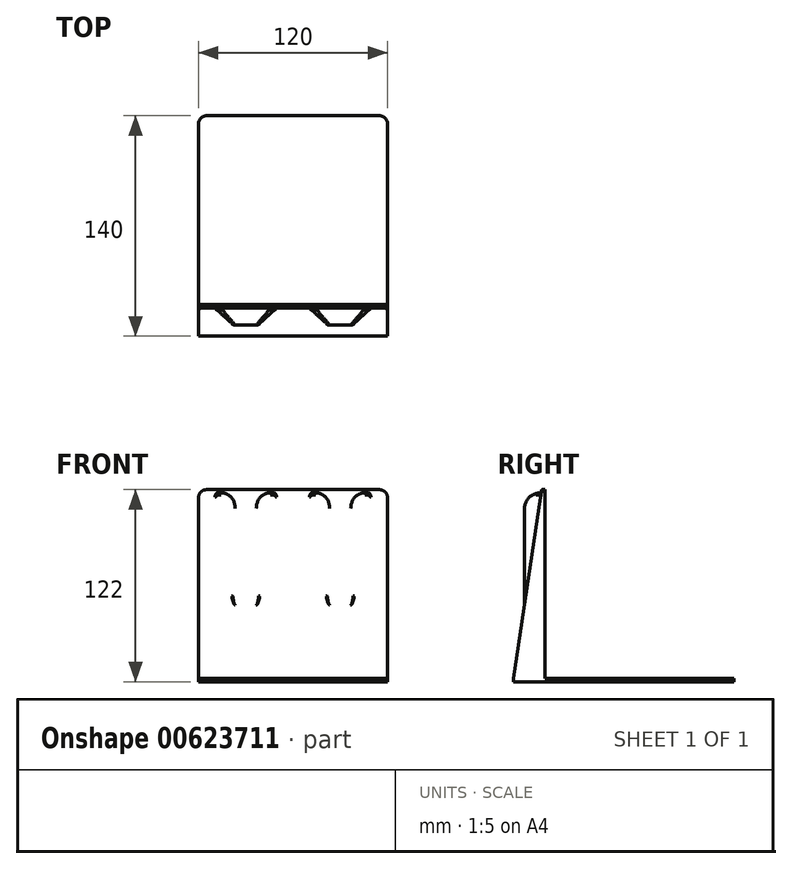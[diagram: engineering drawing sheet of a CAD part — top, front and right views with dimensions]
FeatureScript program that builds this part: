
annotation { "Feature Type Name" : "Feature", "Feature Type Description" : "" }
export const myFeature = defineFeature(function(context is Context, id is Id, definition is map)
    precondition{}
    {
        {
            var Q0;
            Q0=qCreatedBy(makeId("Right.planeOp"),FACE);
            var sketch = newSketch(context, id + "F0", { "sketchPlane" : qUnion([Q0])});
            skLineSegment(sketch, "E0", {"start": v(0, 120) * mm, "end": v(0, 0) * mm});
            skLineSegment(sketch, "E1", {"start": v(0, 0) * mm, "end": v(120, 0) * mm});
            skLineSegment(sketch, "E2", {"start": v(120, 0) * mm, "end": v(120, -2) * mm});
            skLineSegment(sketch, "E3", {"start": v(120, -2) * mm, "end": v(-20, -2) * mm});
            skLineSegment(sketch, "E4", {"start": v(-20, -2) * mm, "end": v(-20, 0) * mm});
            skLineSegment(sketch, "E5", {"start": v(-20, 0) * mm, "end": v(-2, 120) * mm});
            skLineSegment(sketch, "E6", {"start": v(-2, 120) * mm, "end": v(0, 120) * mm});
            skSolve(sketch);
        }
        {
            var Q0;
            Q0=makeQuery(id+"F0.imprint","IMPRINT",FACE,{"disambiguationData":[TD([[makeQuery(id+"F0.imprint","IMPRINT",EDGE,{"derivedFrom":sQuery(id+"F0.wireOp",EDGE,"E0")}),-1.0]])]});
            extrude(context, id + "F1", {"entities" : qUnion([Q0]), "depth" : 120 * mm, "offsetDistance" : 25 * mm});
        }
        {
            var Q0;
            Q0=makeQuery(id+"F1.opExtrude","SWEPT_FACE",FACE,{"disambiguationData":[OSD([sQuery(id+"F0.wireOp",EDGE,"E3")])]});
            var sketch = newSketch(context, id + "F2", { "sketchPlane" : qUnion([Q0])});
            skLineSegment(sketch, "E7.0", {"start": v(120, 20) * mm, "end": v(0, 20) * mm});
            skLineSegment(sketch, "E8.0", {"start": v(0, -120) * mm, "end": v(0, 20) * mm});
            skPoint(sketch, "E9.0", {"position": v(120, 0) * mm});
            skLineSegment(sketch, "E10.0.0", {"start": v(0, 20) * mm, "end": v(0, -120) * mm, "construction": true});
            skLineSegment(sketch, "E10.0.1", {"start": v(0, -120) * mm, "end": v(120, -120) * mm, "construction": true});
            skLineSegment(sketch, "E10.0.2", {"start": v(120, -120) * mm, "end": v(120, 20) * mm, "construction": true});
            skLineSegment(sketch, "E10.0.3", {"start": v(120, 20) * mm, "end": v(0, 20) * mm, "construction": true});
            skLineSegment(sketch, "E11", {"start": v(0, 0) * mm, "end": v(120, 0) * mm, "construction": true});
            skLineSegment(sketch, "E12.0", {"start": v(120, 2) * mm, "end": v(0, 2) * mm, "construction": true});
            skLineSegment(sketch, "E13", {"start": v(8, 0) * mm, "end": v(22.42, 12.99) * mm});
            skLineSegment(sketch, "E14", {"start": v(22.42, 12.99) * mm, "end": v(37.58, 12.99) * mm});
            skLineSegment(sketch, "E15", {"start": v(37.58, 12.99) * mm, "end": v(52, 0) * mm});
            skLineSegment(sketch, "E16", {"start": v(52, 0) * mm, "end": v(8, 0) * mm});
            skLineSegment(sketch, "E17", {"start": v(60, 20) * mm, "end": v(60, -38) * mm, "construction": true});
            skLineSegment(sketch, "E18.MirrorCS", {"start": v(82.42, 12.99) * mm, "end": v(68, 0) * mm});
            skLineSegment(sketch, "E19.MirrorCS", {"start": v(97.58, 12.99) * mm, "end": v(82.42, 12.99) * mm});
            skLineSegment(sketch, "E20.MirrorCS", {"start": v(112, 0) * mm, "end": v(97.58, 12.99) * mm});
            skLineSegment(sketch, "E21.MirrorCS", {"start": v(120, 0) * mm, "end": v(0, 0) * mm, "construction": true});
            skLineSegment(sketch, "E22", {"start": v(68, 0) * mm, "end": v(112, 0) * mm});
            skSolve(sketch);
        }
        {
            var Q0;
            Q0=makeQuery(id+"F2.imprint","IMPRINT",FACE,{"disambiguationData":[TD([[makeQuery(id+"F2.imprint","IMPRINT",EDGE,{"derivedFrom":sQuery(id+"F2.wireOp",EDGE,"E13")}),-1.0]])]});
            var Q1;
            Q1=makeQuery(id+"F2.imprint","IMPRINT",FACE,{"disambiguationData":[TD([[makeQuery(id+"F2.imprint","IMPRINT",EDGE,{"derivedFrom":sQuery(id+"F2.wireOp",EDGE,"E18.MirrorCS")}),1.0]])]});
            extrude(context, id + "F3", {"entities" : qUnion([Q0, Q1]), "operationType" : NewBodyOperationType.ADD, "oppositeDirection" : true, "depth" : 120 * mm, "offsetDistance" : 25 * mm});
        }
        {
            var Q0;
            Q0=makeQuery(id+"F3.opExtrude","CAP_EDGE",EDGE,{"disambiguationData":[OSD([sQuery(id+"F2.wireOp",EDGE,"E19.MirrorCS")])],"isStart":false});
            var Q1;
            Q1=makeQuery(id+"F3.opExtrude","CAP_EDGE",EDGE,{"disambiguationData":[OSD([sQuery(id+"F2.wireOp",EDGE,"E14")])],"isStart":false});
            fillet(context, id + "F4", {"entities" : qUnion([Q0, Q1]), "radius" : 10 * mm, "tangentPropagation" : true, "allowEdgeOverflow" : false});
        }
        {
            var Q0;
            Q0=makeQuery(id+"F3.opExtrude","SWEPT_EDGE",EDGE,{"disambiguationData":[OSD([sQuery(id+"F2.wireOp",EDGE,"E19.MirrorCS"),sQuery(id+"F2.wireOp",EDGE,"E20.MirrorCS")])]});
            var Q1;
            Q1=makeQuery(id+"F3.opExtrude","SWEPT_EDGE",EDGE,{"disambiguationData":[OSD([sQuery(id+"F2.wireOp",EDGE,"E18.MirrorCS"),sQuery(id+"F2.wireOp",EDGE,"E19.MirrorCS")])]});
            var Q2;
            Q2=makeQuery(id+"F3.opExtrude","SWEPT_EDGE",EDGE,{"disambiguationData":[OSD([sQuery(id+"F2.wireOp",EDGE,"E14"),sQuery(id+"F2.wireOp",EDGE,"E15")])]});
            var Q3;
            Q3=makeQuery(id+"F3.opExtrude","SWEPT_EDGE",EDGE,{"disambiguationData":[OSD([sQuery(id+"F2.wireOp",EDGE,"E13"),sQuery(id+"F2.wireOp",EDGE,"E14")])]});
            var Q4;
            Q4=makeQuery(id+"F4.opFillet","BLEND_EDGE",EDGE,{"blendedFrom":[makeQuery(id+"F3.opExtrude","CAP_EDGE",EDGE,{"disambiguationData":[OSD([sQuery(id+"F2.wireOp",EDGE,"E14")])],"isStart":false}),makeQuery(id+"F3.opExtrude","SWEPT_FACE",FACE,{"disambiguationData":[OSD([sQuery(id+"F2.wireOp",EDGE,"E13")])]})],"blendedInto":[makeQuery(id+"F3.opExtrude","SWEPT_FACE",FACE,{"disambiguationData":[OSD([sQuery(id+"F2.wireOp",EDGE,"E13")])]})]});
            var Q5;
            Q5=makeQuery(id+"F4.opFillet","BLEND_EDGE",EDGE,{"blendedFrom":[makeQuery(id+"F3.opExtrude","CAP_EDGE",EDGE,{"disambiguationData":[OSD([sQuery(id+"F2.wireOp",EDGE,"E14")])],"isStart":false}),makeQuery(id+"F3.opExtrude","SWEPT_FACE",FACE,{"disambiguationData":[OSD([sQuery(id+"F2.wireOp",EDGE,"E15")])]})],"blendedInto":[makeQuery(id+"F3.opExtrude","SWEPT_FACE",FACE,{"disambiguationData":[OSD([sQuery(id+"F2.wireOp",EDGE,"E15")])]})]});
            var Q6;
            Q6=makeQuery(id+"F4.opFillet","BLEND_EDGE",EDGE,{"blendedFrom":[makeQuery(id+"F3.opExtrude","CAP_EDGE",EDGE,{"disambiguationData":[OSD([sQuery(id+"F2.wireOp",EDGE,"E19.MirrorCS")])],"isStart":false}),makeQuery(id+"F3.opExtrude","SWEPT_FACE",FACE,{"disambiguationData":[OSD([sQuery(id+"F2.wireOp",EDGE,"E18.MirrorCS")])]})],"blendedInto":[makeQuery(id+"F3.opExtrude","SWEPT_FACE",FACE,{"disambiguationData":[OSD([sQuery(id+"F2.wireOp",EDGE,"E18.MirrorCS")])]})]});
            var Q7;
            Q7=makeQuery(id+"F4.opFillet","BLEND_EDGE",EDGE,{"blendedFrom":[makeQuery(id+"F3.opExtrude","CAP_EDGE",EDGE,{"disambiguationData":[OSD([sQuery(id+"F2.wireOp",EDGE,"E19.MirrorCS")])],"isStart":false}),makeQuery(id+"F3.opExtrude","SWEPT_FACE",FACE,{"disambiguationData":[OSD([sQuery(id+"F2.wireOp",EDGE,"E20.MirrorCS")])]})],"blendedInto":[makeQuery(id+"F3.opExtrude","SWEPT_FACE",FACE,{"disambiguationData":[OSD([sQuery(id+"F2.wireOp",EDGE,"E20.MirrorCS")])]})]});
            fillet(context, id + "F5", {"entities" : qUnion([Q0, Q1, Q2, Q3, Q4, Q5, Q6, Q7]), "radius" : 2.4 * mm, "tangentPropagation" : true, "allowEdgeOverflow" : false});
        }
        {
            var Q0;
            Q0=makeQuery(id+"F3.boolean.opBoolean","INTERSECT",EDGE,{"derivedFrom":[makeQuery(id+"F1.opExtrude","SWEPT_FACE",FACE,{"disambiguationData":[OSD([sQuery(id+"F0.wireOp",EDGE,"E5")])]}),makeQuery(id+"F3.opExtrude","SWEPT_FACE",FACE,{"disambiguationData":[OSD([sQuery(id+"F2.wireOp",EDGE,"E20.MirrorCS")])]})]});
            var Q1;
            Q1=makeQuery(id+"F3.boolean.opBoolean","INTERSECT",EDGE,{"derivedFrom":[makeQuery(id+"F1.opExtrude","SWEPT_FACE",FACE,{"disambiguationData":[OSD([sQuery(id+"F0.wireOp",EDGE,"E5")])]}),makeQuery(id+"F3.opExtrude","SWEPT_FACE",FACE,{"disambiguationData":[OSD([sQuery(id+"F2.wireOp",EDGE,"E18.MirrorCS")])]})]});
            var Q2;
            Q2=makeQuery(id+"F3.boolean.opBoolean","INTERSECT",EDGE,{"derivedFrom":[makeQuery(id+"F1.opExtrude","SWEPT_FACE",FACE,{"disambiguationData":[OSD([sQuery(id+"F0.wireOp",EDGE,"E5")])]}),makeQuery(id+"F3.opExtrude","SWEPT_FACE",FACE,{"disambiguationData":[OSD([sQuery(id+"F2.wireOp",EDGE,"E15")])]})]});
            var Q3;
            Q3=makeQuery(id+"F3.boolean.opBoolean","INTERSECT",EDGE,{"derivedFrom":[makeQuery(id+"F1.opExtrude","SWEPT_FACE",FACE,{"disambiguationData":[OSD([sQuery(id+"F0.wireOp",EDGE,"E5")])]}),makeQuery(id+"F3.opExtrude","SWEPT_FACE",FACE,{"disambiguationData":[OSD([sQuery(id+"F2.wireOp",EDGE,"E13")])]})]});
            fillet(context, id + "F6", {"entities" : qUnion([Q0, Q1, Q2, Q3]), "radius" : 1 * mm, "tangentPropagation" : true, "allowEdgeOverflow" : false});
        }
        {
            var Q0;
            Q0=makeQuery(id+"F1.opExtrude","CAP_EDGE",EDGE,{"disambiguationData":[OSD([sQuery(id+"F0.wireOp",EDGE,"E2")])],"isStart":false});
            var Q1;
            Q1=makeQuery(id+"F1.opExtrude","CAP_EDGE",EDGE,{"disambiguationData":[OSD([sQuery(id+"F0.wireOp",EDGE,"E2")])],"isStart":true});
            fillet(context, id + "F7", {"entities" : qUnion([Q0, Q1]), "radius" : 5 * mm, "tangentPropagation" : true, "allowEdgeOverflow" : false});
        }
        {
            var Q0;
            Q0=makeQuery(id+"F1.opExtrude","CAP_EDGE",EDGE,{"disambiguationData":[OSD([sQuery(id+"F0.wireOp",EDGE,"E6")])],"isStart":false});
            var Q1;
            Q1=makeQuery(id+"F1.opExtrude","CAP_EDGE",EDGE,{"disambiguationData":[OSD([sQuery(id+"F0.wireOp",EDGE,"E6")])],"isStart":true});
            fillet(context, id + "F8", {"entities" : qUnion([Q0, Q1]), "radius" : 5 * mm, "tangentPropagation" : true, "allowEdgeOverflow" : false});
        }
    });
